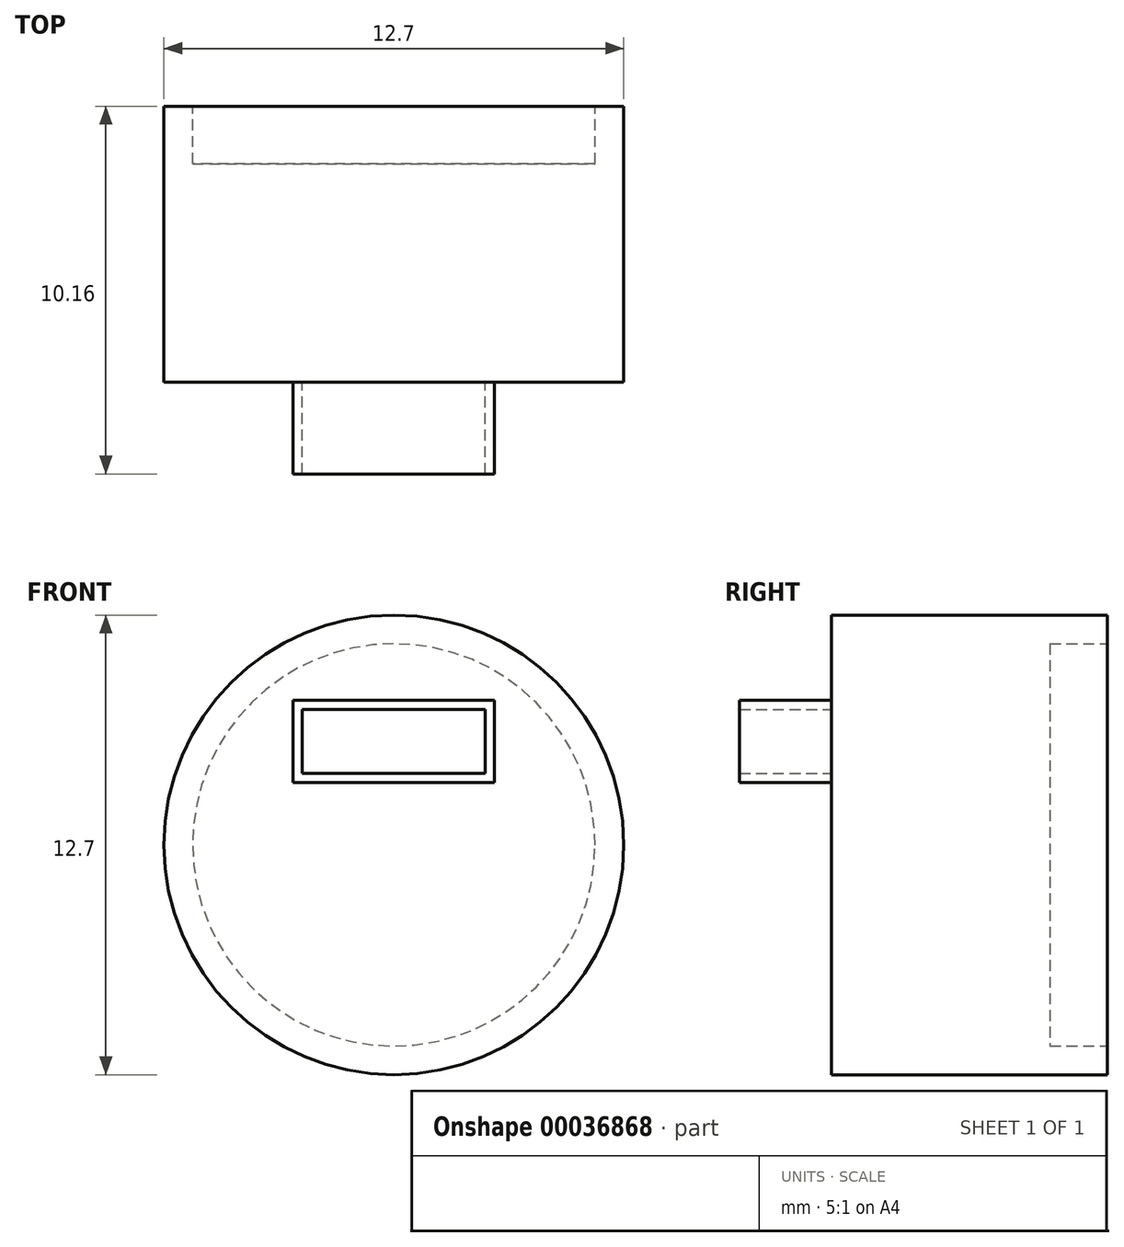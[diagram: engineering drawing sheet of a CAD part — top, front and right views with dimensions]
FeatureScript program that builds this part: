
annotation { "Feature Type Name" : "Feature", "Feature Type Description" : "" }
export const myFeature = defineFeature(function(context is Context, id is Id, definition is map)
    precondition{}
    {
        {
            var Q0;
            Q0=qCreatedBy(makeId("Front.planeOp"),FACE);
            var sketch = newSketch(context, id + "F0", { "sketchPlane" : qUnion([Q0])});
            skCircle(sketch, "E0", {"center": v(0, 0) * mm, "radius": 6.35 * mm});
            skSolve(sketch);
        }
        {
            var Q0;
            Q0=makeQuery(id+"F0.imprint","IMPRINT",FACE,{"disambiguationData":[TD([[makeQuery(id+"F0.imprint","IMPRINT",EDGE,{"derivedFrom":sQuery(id+"F0.wireOp",EDGE,"E0")}),1.0]])]});
            var Q1;
            Q1=sQuery(id+"F0.wireOp",EDGE,"E0");
            extrude(context, id + "F1", {"entities" : qUnion([Q0]), "surfaceEntities" : qUnion([Q1]), "depth" : 7.62 * mm});
        }
        {
            var Q0;
            Q0=makeQuery(id+"F1.opExtrude","CAP_FACE",FACE,{"disambiguationData":[OSD([sQuery(id+"F0.wireOp",EDGE,"E0")])],"isStart":true});
            var sketch = newSketch(context, id + "F2", { "sketchPlane" : qUnion([Q0])});
            skCircle(sketch, "E1.0", {"center": v(0, 0) * mm, "radius": 6.35 * mm, "construction": true});
            skCircle(sketch, "E2.0", {"center": v(0, 0) * mm, "radius": 5.56 * mm});
            skSolve(sketch);
        }
        {
            var Q0;
            Q0 = qSketchRegion(id + "F2", true);
            extrude(context, id + "F3", {"entities" : qUnion([Q0]), "operationType" : NewBodyOperationType.REMOVE, "oppositeDirection" : true, "depth" : 1.59 * mm});
        }
        {
            var Q0;
            Q0=makeQuery(id+"F1.opExtrude","CAP_FACE",FACE,{"disambiguationData":[OSD([sQuery(id+"F0.wireOp",EDGE,"E0")])],"isStart":false});
            var sketch = newSketch(context, id + "F4", { "sketchPlane" : qUnion([Q0])});
            skLineSegment(sketch, "E3.rect.bottom", {"start": v(2.53, 3.74) * mm, "end": v(-2.53, 3.74) * mm});
            skLineSegment(sketch, "E3.rect.top", {"start": v(2.53, 1.97) * mm, "end": v(-2.53, 1.97) * mm});
            skLineSegment(sketch, "E3.rect.left", {"start": v(2.53, 3.74) * mm, "end": v(2.53, 1.97) * mm});
            skLineSegment(sketch, "E3.rect.right", {"start": v(-2.53, 3.74) * mm, "end": v(-2.53, 1.97) * mm});
            skPoint(sketch, "E3.rect.middle", {"position": v(0, 2.86) * mm});
            skLineSegment(sketch, "E4.0", {"start": v(-2.78, 4) * mm, "end": v(-2.78, 1.72) * mm});
            skLineSegment(sketch, "E4.1", {"start": v(2.78, 4) * mm, "end": v(-2.78, 4) * mm});
            skLineSegment(sketch, "E4.2", {"start": v(2.78, 4) * mm, "end": v(2.78, 1.72) * mm});
            skLineSegment(sketch, "E4.3", {"start": v(2.78, 1.72) * mm, "end": v(-2.78, 1.72) * mm});
            skSolve(sketch);
        }
        {
            var Q0;
            Q0 = qSketchRegion(id + "F4", true);
            extrude(context, id + "F5", {"entities" : qUnion([Q0]), "operationType" : NewBodyOperationType.ADD, "depth" : 2.54 * mm});
        }
    });
